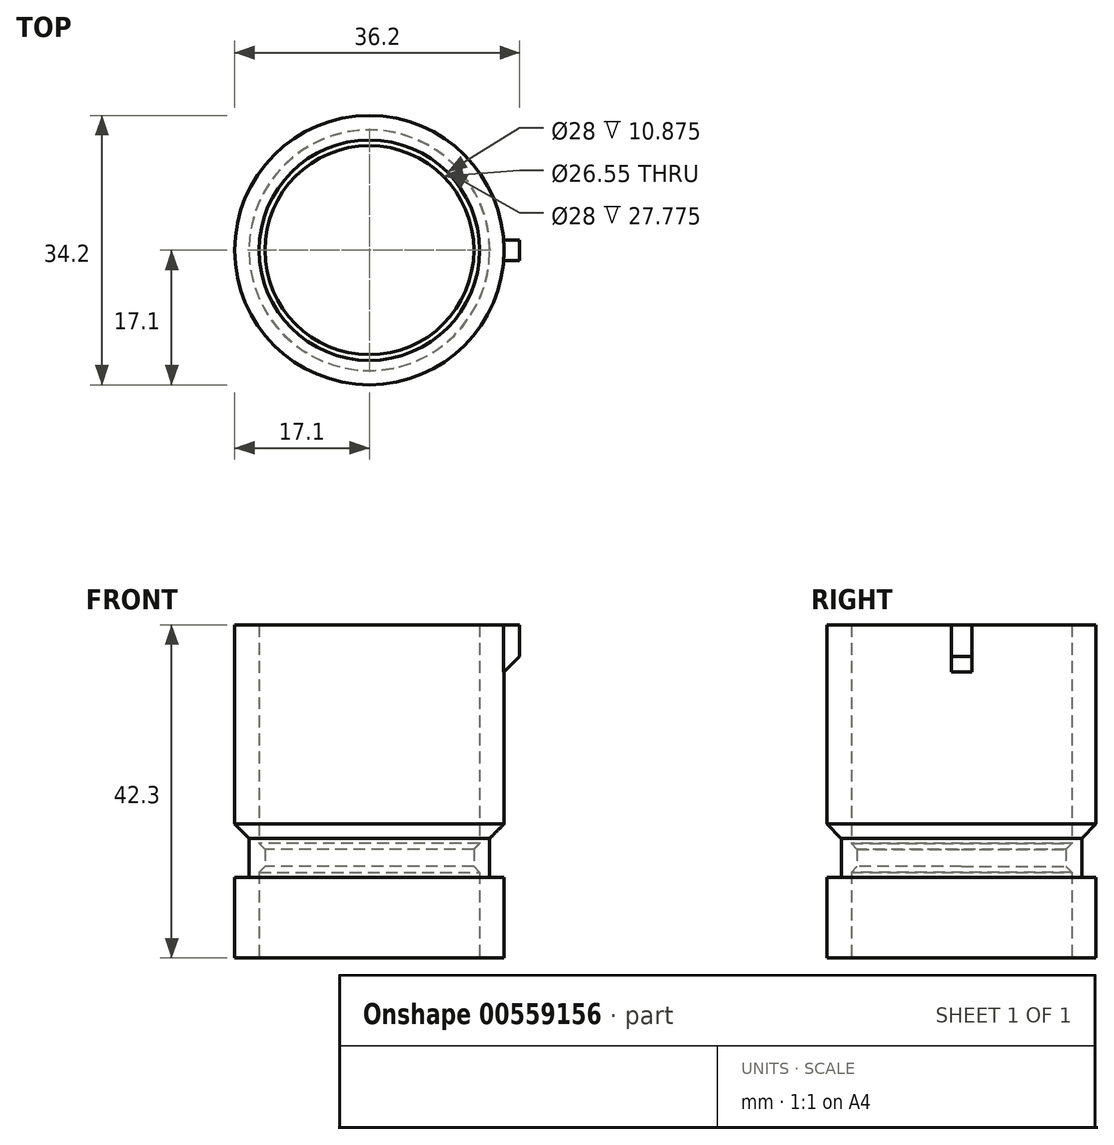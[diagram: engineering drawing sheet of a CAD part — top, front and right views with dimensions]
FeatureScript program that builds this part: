
annotation { "Feature Type Name" : "Feature", "Feature Type Description" : "" }
export const myFeature = defineFeature(function(context is Context, id is Id, definition is map)
    precondition{}
    {
        {
            var Q0;
            Q0=qCreatedBy(makeId("Top.planeOp"),FACE);
            var sketch = newSketch(context, id + "F0", { "sketchPlane" : qUnion([Q0])});
            skCircle(sketch, "E0", {"center": v(0, 0) * mm, "radius": 17.1 * mm});
            skCircle(sketch, "E1", {"center": v(0, 0) * mm, "radius": 14 * mm});
            skSolve(sketch);
        }
        {
            var Q0;
            Q0=makeQuery(id+"F0.imprint","IMPRINT",FACE,{"disambiguationData":[TD([[makeQuery(id+"F0.imprint","IMPRINT",EDGE,{"derivedFrom":sQuery(id+"F0.wireOp",EDGE,"E0")}),1.0]])]});
            extrude(context, id + "F1", {"entities" : qUnion([Q0]), "depth" : 10.2 * mm});
        }
        {
            var Q0;
            Q0=makeQuery(id+"F1.opExtrude","CAP_FACE",FACE,{"disambiguationData":[OSD([sQuery(id+"F0.wireOp",EDGE,"E0"),sQuery(id+"F0.wireOp",EDGE,"E1")])],"isStart":false});
            var sketch = newSketch(context, id + "F2", { "sketchPlane" : qUnion([Q0])});
            skCircle(sketch, "E2", {"center": v(0, 0) * mm, "radius": 15.28 * mm});
            skCircle(sketch, "E3.0", {"center": v(0, 0) * mm, "radius": 13.28 * mm});
            skSolve(sketch);
        }
        {
            var Q0;
            Q0=makeQuery(id+"F2.imprint","IMPRINT",FACE,{"disambiguationData":[TD([[makeQuery(id+"F2.imprint","IMPRINT",EDGE,{"derivedFrom":sQuery(id+"F2.wireOp",EDGE,"E3.0")}),-1.0]])]});
            var Q1;
            Q1=makeQuery(id+"F2.imprint","IMPRINT",FACE,{"disambiguationData":[TD([[makeQuery(id+"F2.imprint","IMPRINT",EDGE,{"derivedFrom":sQuery(id+"F2.wireOp",EDGE,"E2")}),1.0]])]});
            extrude(context, id + "F3", {"entities" : qUnion([Q0, Q1]), "operationType" : NewBodyOperationType.ADD, "depth" : 5 * mm});
        }
        {
            var Q0;
            Q0=makeQuery(id+"F3.opExtrude","CAP_FACE",FACE,{"disambiguationData":[OSD([sQuery(id+"F2.wireOp",EDGE,"E2"),sQuery(id+"F2.wireOp",EDGE,"E3.0")])],"isStart":false});
            var sketch = newSketch(context, id + "F4", { "sketchPlane" : qUnion([Q0])});
            skCircle(sketch, "E4.0.0", {"center": v(0, 0) * mm, "radius": 17.1 * mm});
            skCircle(sketch, "E5.0", {"center": v(0, 0) * mm, "radius": 14 * mm});
            skSolve(sketch);
        }
        {
            var Q0;
            Q0=makeQuery(id+"F4.imprint","IMPRINT",FACE,{"disambiguationData":[TD([[makeQuery(id+"F4.imprint","IMPRINT",EDGE,{"derivedFrom":sQuery(id+"F4.wireOp",EDGE,"E4.0.0")}),1.0]])]});
            var Q1;
            Q1=makeQuery(id+"F4.imprint","IMPRINT",FACE,{"disambiguationData":[TD([[makeQuery(id+"F4.imprint","IMPRINT",EDGE,{"derivedFrom":sQuery(id+"F4.wireOp",EDGE,"E5.0")}),-1.0]])]});
            extrude(context, id + "F5", {"entities" : qUnion([Q0, Q1]), "operationType" : NewBodyOperationType.ADD, "depth" : 27.1 * mm});
        }
        {
            var Q0;
            Q0=makeQuery(id+"F3.opExtrude","CAP_EDGE",EDGE,{"disambiguationData":[OSD([sQuery(id+"F2.wireOp",EDGE,"E3.0")])],"isStart":true});
            var Q1;
            Q1=makeQuery(id+"F3.opExtrude","CAP_EDGE",EDGE,{"disambiguationData":[OSD([sQuery(id+"F2.wireOp",EDGE,"E3.0")])],"isStart":false});
            chamfer(context, id + "F6", {"entities" : qUnion([Q0, Q1]), "width" : 1.4 * mm, "tangentPropagation" : true});
        }
        {
            var Q0;
            Q0=makeQuery(id+"F5.opExtrude","CAP_EDGE",EDGE,{"disambiguationData":[OSD([sQuery(id+"F4.wireOp",EDGE,"E4.0.0")])],"isStart":true});
            chamfer(context, id + "F7", {"entities" : qUnion([Q0]), "width" : 1.8 * mm, "tangentPropagation" : true});
        }
        {
            var Q0;
            Q0=makeQuery(id+"F5.opExtrude","CAP_FACE",FACE,{"disambiguationData":[OSD([sQuery(id+"F4.wireOp",EDGE,"E4.0.0"),sQuery(id+"F4.wireOp",EDGE,"E5.0")])],"isStart":false});
            var sketch = newSketch(context, id + "F8", { "sketchPlane" : qUnion([Q0])});
            skLineSegment(sketch, "E6", {"start": v(0, 0) * mm, "end": v(19.1, 0) * mm});
            skCircle(sketch, "E7.0", {"center": v(0, 0) * mm, "radius": 17.1 * mm, "construction": true});
            skLineSegment(sketch, "E8.bottom", {"start": v(19.1, 0) * mm, "end": v(16.47, 0) * mm});
            skLineSegment(sketch, "E8.top", {"start": v(19.1, 1.3) * mm, "end": v(16.47, 1.3) * mm});
            skLineSegment(sketch, "E8.left", {"start": v(19.1, 0) * mm, "end": v(19.1, 1.3) * mm});
            skLineSegment(sketch, "E8.right", {"start": v(16.47, 0) * mm, "end": v(16.47, 1.3) * mm});
            skPoint(sketch, "E9.oppositeSnap0", {"position": v(16.47, 0.65) * mm});
            skLineSegment(sketch, "E9.top", {"start": v(19.1, -1.3) * mm, "end": v(16.47, -1.3) * mm});
            skLineSegment(sketch, "E9.left", {"start": v(19.1, 0) * mm, "end": v(19.1, -1.3) * mm});
            skLineSegment(sketch, "E9.right", {"start": v(16.47, 0) * mm, "end": v(16.47, -1.3) * mm});
            skLineSegment(sketch, "E10", {"start": v(17.05, 1.3) * mm, "end": v(17.05, -1.3) * mm});
            skSolve(sketch);
        }
        {
            var Q0;
            {var subQ0=sQuery(id+"F8.wireOp",EDGE,"E8.left");Q0=makeQuery(id+"F8.imprint","IMPRINT",FACE,{"disambiguationData":[TD([[makeQuery(id+"F8.imprint","IMPRINT",EDGE,{"derivedFrom":subQ0}),1.0]])]});}
            var Q1;
            {var subQ0=sQuery(id+"F8.wireOp",EDGE,"E9.left");Q1=makeQuery(id+"F8.imprint","IMPRINT",FACE,{"disambiguationData":[TD([[makeQuery(id+"F8.imprint","IMPRINT",EDGE,{"derivedFrom":subQ0}),-1.0]])]});}
            var Q2;
            {var subQ0=sQuery(id+"F8.wireOp",EDGE,"E10");var subQ1=sQuery(id+"F8.wireOp",EDGE,"E8.bottom");var subQ2=makeQuery(id+"F8.imprint","INTERSECT",VERTEX,{"derivedFrom":[subQ1,subQ0]});Q2=makeQuery(id+"F8.imprint","IMPRINT",FACE,{"disambiguationData":[TD([[makeQuery(id+"F8.imprint","IMPRINT",EDGE,{"disambiguationData":[TD([[subQ2,1.0]])],"derivedFrom":subQ1}),-1.0]])]});}
            var Q3;
            {var subQ0=sQuery(id+"F8.wireOp",EDGE,"E10");var subQ1=sQuery(id+"F8.wireOp",EDGE,"E8.bottom");var subQ2=makeQuery(id+"F8.imprint","INTERSECT",VERTEX,{"derivedFrom":[subQ1,subQ0]});Q3=makeQuery(id+"F8.imprint","IMPRINT",FACE,{"disambiguationData":[TD([[makeQuery(id+"F8.imprint","IMPRINT",EDGE,{"disambiguationData":[TD([[subQ2,1.0]])],"derivedFrom":subQ1}),1.0]])]});}
            extrude(context, id + "F9", {"entities" : qUnion([Q0, Q1, Q2, Q3]), "oppositeDirection" : true, "depth" : 6 * mm});
        }
        {
            var Q0;
            Q0=makeQuery(id+"F9.opExtrude","CAP_EDGE",EDGE,{"disambiguationData":[OSD([sQuery(id+"F8.wireOp",EDGE,"E8.left"),sQuery(id+"F8.wireOp",EDGE,"E9.left")])],"isStart":false});
            chamfer(context, id + "F10", {"entities" : qUnion([Q0]), "width" : 2 * mm, "tangentPropagation" : true});
        }
    });
